# Revit family: Lighting-Industriale-GEWISS-SMART[3]e-PLAFONIERA-LED_TRASPARENTE_1200mm
name_source: partatom
category: Apparecchi per illuminazione
units: mm (PartAtom-declared; Revit-internal decimal feet)

## family parameters
Condiviso = No
Host = Superficie
Punto di calcolo locali = Sì
Quota connettore circolare = Usa diametro
Sorgente d'illuminazione = No
Taglio con vuoti quando caricato = No
Tipo di parte = Normale

## types (1)
- Lighting-Industriale-GEWISS-SMART[3]e-PLAFONIERA-LED_TRASPARENTE_1200mm
    Alimentatore = Incluso
    Apparecchio a ridotta temperatura superficiale = Si
    Applicazione = Interno
    Cablaggio = Con connettore stagno Gw connect
    Cablaggio : = Stand alone
    Caratteristiche elettriche e gestione della luce = -
    Caratteristiche ottiche e illuminotecniche = -
    Catalogo = LIGHTING
    Certificazione DIN 18032-3 = Non disponibile
    Certificazioni e classificazioni = -
    Classe fotobiologica = -
    Classe isolamento = II
    Classificazione: = -
    Codice digitale univoco (Datamatrix) = Datamatrix
    Colore = Grigio RAL 7035
    Contesto = Illuminazione di magazzini, parcheggi coperti e locali produttivi industriali
    Controllo abbagliamento e luminanza = -
    Corpo = Policarbonato
    Descrizione = SMART3e 1200 ON/OFF TRASP CRI80 4000K
    Dispositivo di protezione = DM 1KV / CM 2KV
    Durata di vita = L80B20(Tq25°C)=90.000h - L80B20(Tq40°C)=50.000h
    Failure rate alimentatore = F10 = 90.000 h a Tq 25°C/F10= 50.000 h a Tq 40°C
    Finitura colore = PC colorato in pasta RAL7035
    Fissaggio = Supporto in acciaio INOX
    Frequenza nominale (Hz) = 50/60 Hz
    Ganci = GEWISS  - ALLUMINIO
    Gancio di chiusura = -
    Garanzia = 5 anni
    Grado di protezione = IP66/IP69
    Gruppo ottico = Integrato nello schermo
    Guarnizioni = Sigillante depositato a CNC
    IDF = 9517fd0f-6083-4c82-8e58-1fa8055cc39e
    IDT = 55c9cc56-a650-4216-8e8d-8a519f427575
    IPEA = -
    Immagine tipo = GWS3136T.jpg
    Inclinazione = Con staffa di fissaggio
    Indice di resa cromatica = CRI>80
    Informazioni generali = -
    Installazione e manutenzione = -
    Lampada = LED
    Lunghezza Lampada = 1200 mm
    Materiali = -
    Modello = GWS3220ET840
    Norma di riferimento = EN60598-1; IEC 62778; IEC62471
    Ottica = Trasparente microprismato
    Produttore = GEWISS S.p.A.
    Prospetto di default = 1219 mm
    Resistenza agli urti = IK08
    Resistenza al filo incandescente = 850 °C
    Scheda Tecnica = https://www.gewiss.com
    Schermo = Policarbonato stabilizzato agli UV
    Schermo- = Gewiss - Led Acceso
    Sistema di controllo = Stand Alone - On / Off
    Sistema di controllo : = ON / OFF
    Sostituibilità gruppo ottico = Non disponibile
    Sostituibilità piastra di cablaggio = Non disponibile
    Stampa 1_100 = Sì
    Stampa 1_200 = No
    Struttura = GEWISS - SMART 3 - GRIGIO
    Superficie massima esposta al vento : = -
    Temperatura di esercizio = -25 +40 °C
    Temperatura di stoccaggio = -25 +80 °C
    Tensione di alimentazione = 220 - 240 V
    Tipo di apparecchio = Apparecchio a LED per illuminazione generale
    Tipo di installazione e montaggio = Plafone - Parete - Sospensione
    Tipologia sorgente luminosa = LED - Non sostituibile
    Tolleranza cromatica = SDCM = 3
    URL = https://www.gewiss.com
    Vano di alimentazione = Integrato
    Versione file RFA = 21.4
    Viti esterne = -
